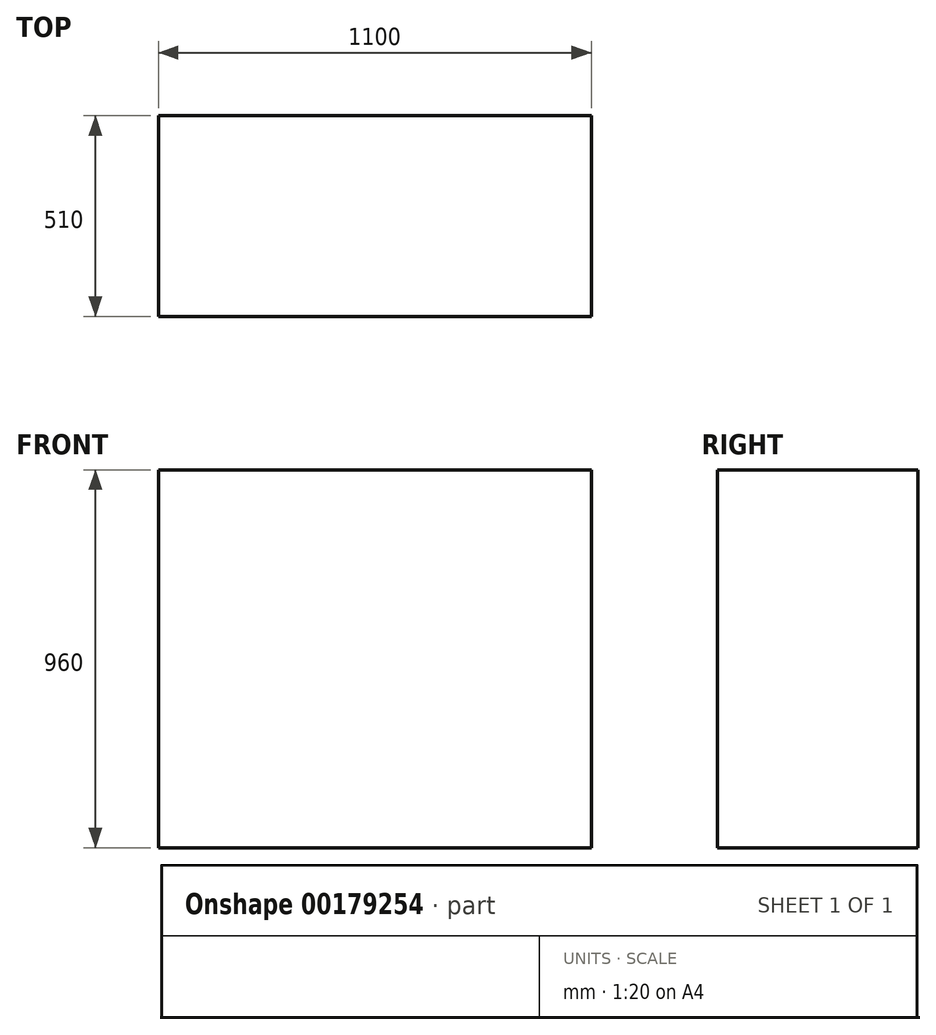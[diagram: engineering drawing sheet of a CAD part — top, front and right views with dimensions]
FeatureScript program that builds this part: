
annotation { "Feature Type Name" : "Feature", "Feature Type Description" : "" }
export const myFeature = defineFeature(function(context is Context, id is Id, definition is map)
    precondition{}
    {
        {
            var Q0;
            Q0=qCreatedBy(makeId("Top.planeOp"),FACE);
            var sketch = newSketch(context, id + "F0", { "sketchPlane" : qUnion([Q0])});
            skLineSegment(sketch, "E0.bottom", {"start": v(-550, -255) * mm, "end": v(550, -255) * mm});
            skLineSegment(sketch, "E0.top", {"start": v(-550, 255) * mm, "end": v(550, 255) * mm});
            skLineSegment(sketch, "E0.left", {"start": v(-550, -255) * mm, "end": v(-550, 255) * mm});
            skLineSegment(sketch, "E0.right", {"start": v(550, -255) * mm, "end": v(550, 255) * mm});
            skPoint(sketch, "E0.middle", {"position": v(0, 0) * mm});
            skSolve(sketch);
        }
        {
            var Q0;
            Q0 = qSketchRegion(id + "F0", true);
            extrude(context, id + "F1", {"entities" : qUnion([Q0]), "depth" : 960 * mm});
        }
    });
